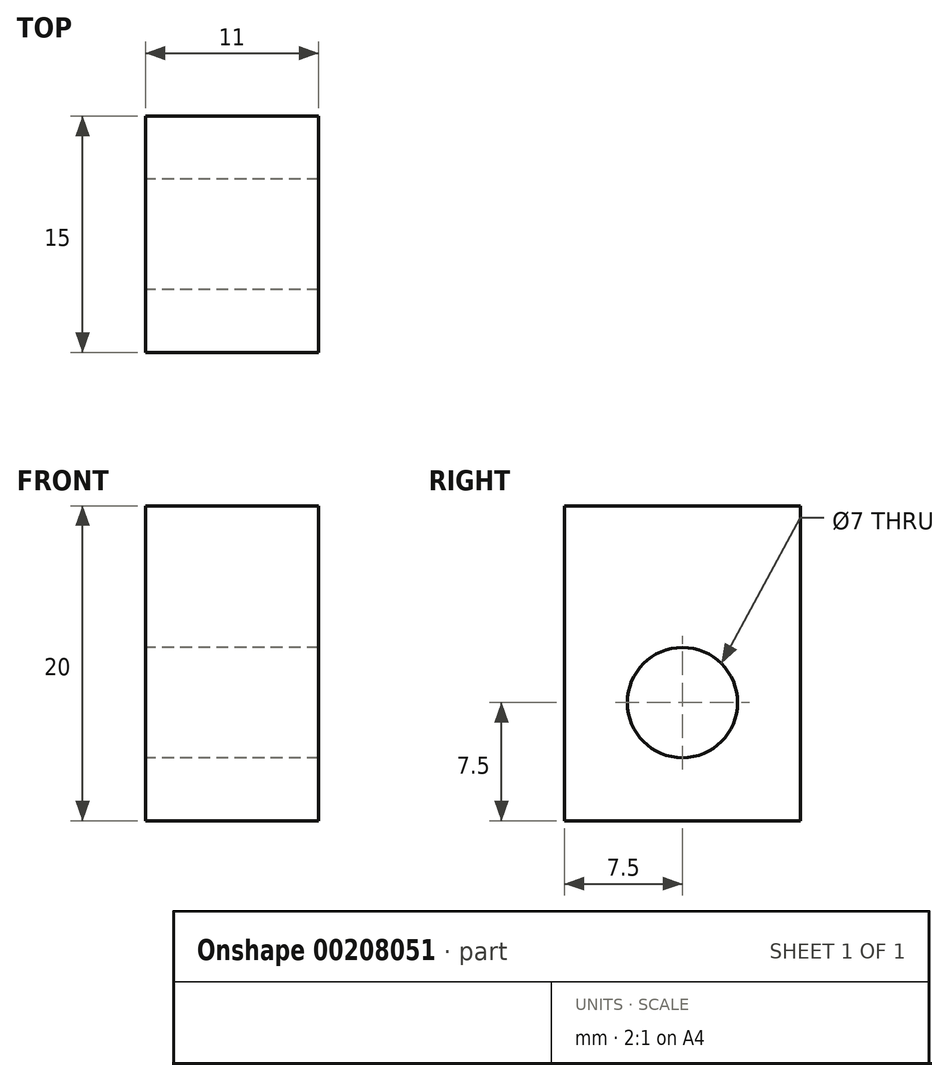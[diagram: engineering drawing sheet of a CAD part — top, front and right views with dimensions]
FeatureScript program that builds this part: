
annotation { "Feature Type Name" : "Feature", "Feature Type Description" : "" }
export const myFeature = defineFeature(function(context is Context, id is Id, definition is map)
    precondition{}
    {
        {
            var Q0;
            Q0=qCreatedBy(makeId("Top.planeOp"),FACE);
            var sketch = newSketch(context, id + "F0", { "sketchPlane" : qUnion([Q0])});
            skLineSegment(sketch, "E0.bottom", {"start": v(5.5, -7.5) * mm, "end": v(-5.5, -7.5) * mm});
            skLineSegment(sketch, "E0.top", {"start": v(5.5, 7.5) * mm, "end": v(-5.5, 7.5) * mm});
            skLineSegment(sketch, "E0.left", {"start": v(5.5, -7.5) * mm, "end": v(5.5, 7.5) * mm});
            skLineSegment(sketch, "E0.right", {"start": v(-5.5, -7.5) * mm, "end": v(-5.5, 7.5) * mm});
            skPoint(sketch, "E0.middle", {"position": v(0, 0) * mm});
            skSolve(sketch);
        }
        {
            var Q0;
            Q0=qCreatedBy(makeId("Top.planeOp"),FACE);
            var sketch = newSketch(context, id + "F1", { "sketchPlane" : qUnion([Q0])});
            skArc(sketch, "E1", {"start": v(6.59, 7.52) * mm, "mid": v(-8.96, -4.43) * mm, "end": v(9.98, 0.66) * mm});
            skArc(sketch, "E2", {"start": v(7.9, 9.03) * mm, "mid": v(-10.76, -5.32) * mm, "end": v(11.97, 0.8) * mm});
            skLineSegment(sketch, "E3", {"start": v(0, 0) * mm, "end": v(7.9, 9.03) * mm});
            skLineSegment(sketch, "E4", {"start": v(0, 0) * mm, "end": v(11.97, 0.8) * mm});
            skSolve(sketch);
        }
        {
            var Q0;
            Q0=makeQuery(id+"F0.imprint","IMPRINT",FACE,{"disambiguationData":[TD([[makeQuery(id+"F0.imprint","IMPRINT",EDGE,{"derivedFrom":sQuery(id+"F0.wireOp",EDGE,"E0.bottom")}),-1.0]])]});
            extrude(context, id + "F2", {"entities" : qUnion([Q0]), "depth" : 20 * mm});
        }
        {
            var Q0;
            Q0=makeQuery(id+"F1.imprint","IMPRINT",FACE,{"disambiguationData":[TD([[makeQuery(id+"F1.imprint","IMPRINT",EDGE,{"derivedFrom":sQuery(id+"F1.wireOp",EDGE,"E1")}),-1.0]])]});
            extrude(context, id + "F3", {"entities" : qUnion([Q0]), "depth" : 19 * mm});
        }
        {
            var Q0;
            Q0=makeQuery(id+"F2.opExtrude","SWEPT_FACE",FACE,{"disambiguationData":[OSD([sQuery(id+"F0.wireOp",EDGE,"E0.right")])]});
            cPlane(context, id + "F4", {"entities" : qUnion([Q0]), "cplaneType" : CPlaneType.OFFSET, "offset" : 0 * mm, "width" : 150 * mm, "height" : 150 * mm});
        }
        {
            var Q0;
            Q0=qCreatedBy(id+"F4.planeOp",FACE);
            var sketch = newSketch(context, id + "F5", { "sketchPlane" : qUnion([Q0])});
            skLineSegment(sketch, "E5", {"start": v(0, 0) * mm, "end": v(0, 7.5) * mm});
            skCircle(sketch, "E6", {"center": v(0, 7.5) * mm, "radius": 3.5 * mm});
            skSolve(sketch);
        }
        {
            var Q0;
            Q0=makeQuery(id+"F5.imprint","IMPRINT",FACE,{"disambiguationData":[TD([[makeQuery(id+"F5.imprint","IMPRINT",EDGE,{"derivedFrom":sQuery(id+"F5.wireOp",EDGE,"E6")}),1.0]])]});
            extrude(context, id + "F6", {"entities" : qUnion([Q0]), "operationType" : NewBodyOperationType.REMOVE, "oppositeDirection" : true, "depth" : 15 * mm});
        }
        {
            var Q0;
            Q0=makeQuery(id+"F3.opExtrude","SWEPT_BODY",BODY,{"disambiguationData":[OSD([sQuery(id+"F1.wireOp",EDGE,"E1"),sQuery(id+"F1.wireOp",EDGE,"E2"),sQuery(id+"F1.wireOp",EDGE,"E3"),sQuery(id+"F1.wireOp",EDGE,"E4")])]});
            deleteBodies(context, id + "F7", {"entities" : qUnion([Q0])});
        }
        {
            var Q0;
            Q0=makeQuery(id+"F2.opExtrude","CAP_FACE",FACE,{"disambiguationData":[OSD([sQuery(id+"F0.wireOp",EDGE,"E0.bottom"),sQuery(id+"F0.wireOp",EDGE,"E0.top"),sQuery(id+"F0.wireOp",EDGE,"E0.left"),sQuery(id+"F0.wireOp",EDGE,"E0.right")])],"isStart":false});
            cPlane(context, id + "F8", {"entities" : qUnion([Q0]), "cplaneType" : CPlaneType.OFFSET, "offset" : 0 * mm, "width" : 150 * mm, "height" : 150 * mm});
        }
    });
